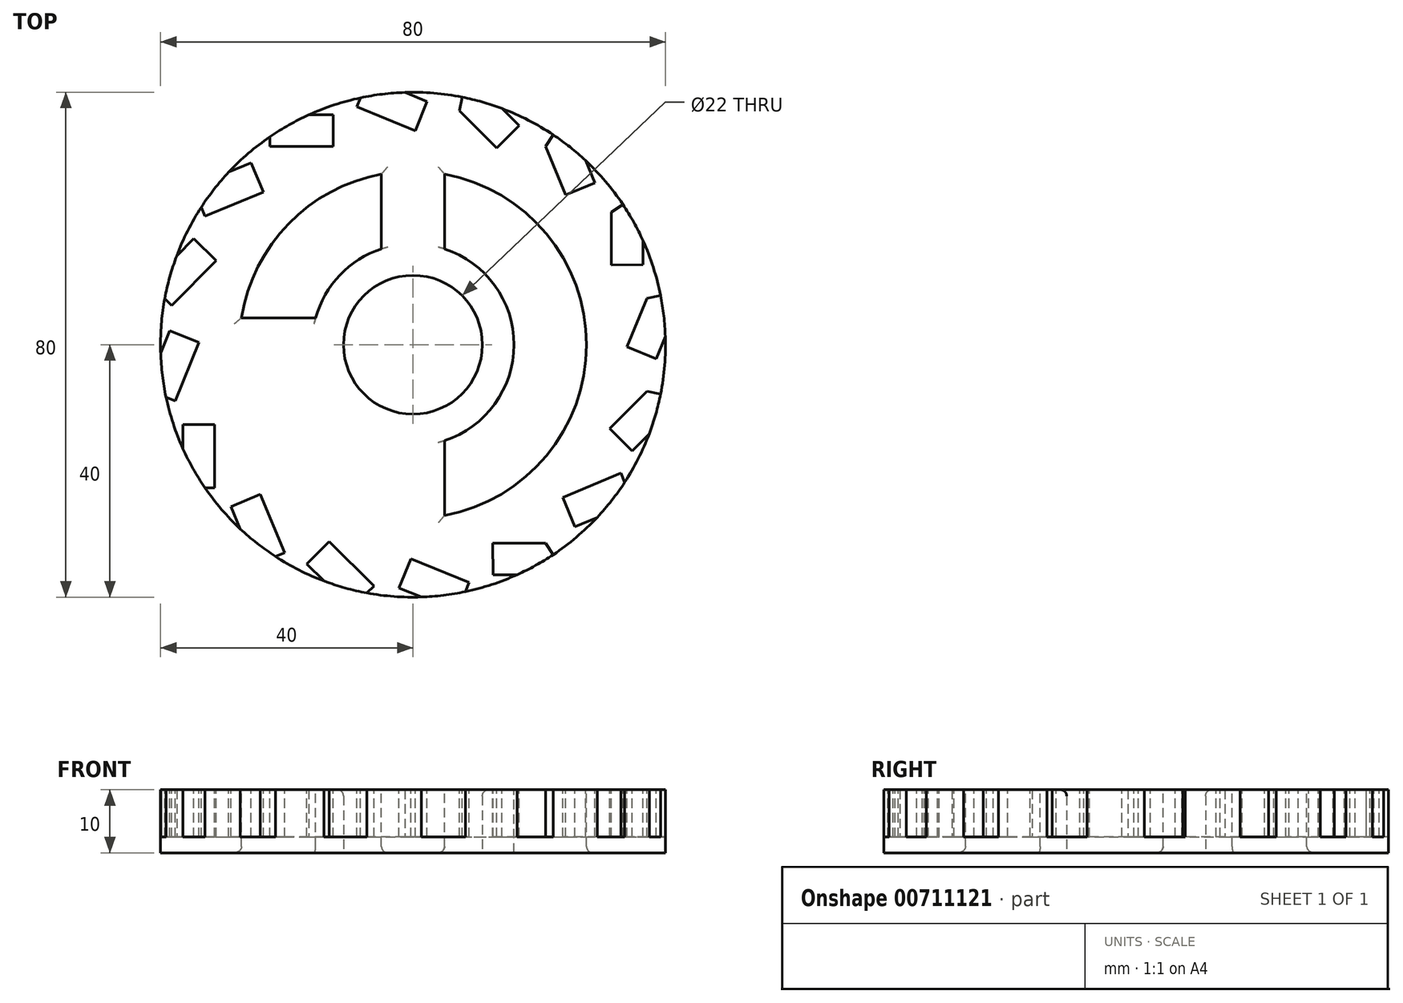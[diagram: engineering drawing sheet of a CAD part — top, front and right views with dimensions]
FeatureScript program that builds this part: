
annotation { "Feature Type Name" : "Feature", "Feature Type Description" : "" }
export const myFeature = defineFeature(function(context is Context, id is Id, definition is map)
    precondition{}
    {
        {
            var Q0;
            Q0=qCreatedBy(makeId("Front.planeOp"),FACE);
            var sketch = newSketch(context, id + "F0", { "sketchPlane" : qUnion([Q0])});
            skLineSegment(sketch, "E0.bottom", {"start": v(0, 0) * mm, "end": v(40, 0) * mm});
            skLineSegment(sketch, "E0.top", {"start": v(0, 10) * mm, "end": v(40, 10) * mm});
            skLineSegment(sketch, "E0.left", {"start": v(0, 0) * mm, "end": v(0, 10) * mm});
            skLineSegment(sketch, "E0.right", {"start": v(40, 0) * mm, "end": v(40, 10) * mm});
            skSolve(sketch);
        }
        {
            var Q0;
            Q0=makeQuery(id+"F0.imprint","IMPRINT",FACE,{"disambiguationData":[TD([[makeQuery(id+"F0.imprint","IMPRINT",EDGE,{"derivedFrom":sQuery(id+"F0.wireOp",EDGE,"E0.bottom")}),1.0]])]});
            var Q1;
            Q1=sQuery(id+"F0.wireOp",EDGE,"E0.left");
            revolve(context, id + "F1", {"surfaceOperationType" : NewSurfaceOperationType.NEW, "entities" : qUnion([Q0]), "axis" : qUnion([Q1]), "revolveType" : RevolveType.FULL});
        }
        {
            var Q0;
            Q0=makeQuery(id+"F1.opRevolve","SWEPT_FACE",FACE,{"disambiguationData":[OSD([sQuery(id+"F0.wireOp",EDGE,"E0.bottom")])]});
            var sketch = newSketch(context, id + "F2", { "sketchPlane" : qUnion([Q0])});
            skCircle(sketch, "E1", {"center": v(0, 0) * mm, "radius": 11 * mm});
            skSolve(sketch);
        }
        {
            var Q0;
            Q0=makeQuery(id+"F2.imprint","IMPRINT",FACE,{"disambiguationData":[TD([[makeQuery(id+"F2.imprint","IMPRINT",EDGE,{"derivedFrom":sQuery(id+"F2.wireOp",EDGE,"E1")}),1.0]])]});
            extrude(context, id + "F3", {"entities" : qUnion([Q0]), "operationType" : NewBodyOperationType.REMOVE, "oppositeDirection" : true, "depth" : 25 * mm, "offsetDistance" : 25 * mm});
        }
        {
            var Q0;
            Q0=makeQuery(id+"F1.opRevolve","SWEPT_FACE",FACE,{"disambiguationData":[OSD([sQuery(id+"F0.wireOp",EDGE,"E0.top")])]});
            var sketch = newSketch(context, id + "F4", { "sketchPlane" : qUnion([Q0])});
            skCircle(sketch, "E2.cCircle", {"center": v(0, 0) * mm, "radius": 40 * mm, "construction": true});
            skLineSegment(sketch, "E2.0", {"start": v(-7.96, 40) * mm, "end": v(7.96, 40) * mm});
            skLineSegment(sketch, "E2.1", {"start": v(7.96, 40) * mm, "end": v(22.66, 33.91) * mm});
            skLineSegment(sketch, "E2.2", {"start": v(22.66, 33.91) * mm, "end": v(33.91, 22.66) * mm});
            skLineSegment(sketch, "E2.3", {"start": v(33.91, 22.66) * mm, "end": v(40, 7.96) * mm});
            skLineSegment(sketch, "E2.4", {"start": v(40, 7.96) * mm, "end": v(40, -7.96) * mm});
            skLineSegment(sketch, "E2.5", {"start": v(40, -7.96) * mm, "end": v(33.91, -22.66) * mm});
            skLineSegment(sketch, "E2.6", {"start": v(33.91, -22.66) * mm, "end": v(22.66, -33.91) * mm});
            skLineSegment(sketch, "E2.7", {"start": v(22.66, -33.91) * mm, "end": v(7.96, -40) * mm});
            skLineSegment(sketch, "E2.8", {"start": v(7.96, -40) * mm, "end": v(-7.96, -40) * mm});
            skLineSegment(sketch, "E2.9", {"start": v(-7.96, -40) * mm, "end": v(-22.66, -33.91) * mm});
            skLineSegment(sketch, "E2.10", {"start": v(-22.66, -33.91) * mm, "end": v(-33.91, -22.66) * mm});
            skLineSegment(sketch, "E2.11", {"start": v(-33.91, -22.66) * mm, "end": v(-40, -7.96) * mm});
            skLineSegment(sketch, "E2.12", {"start": v(-40, -7.96) * mm, "end": v(-40, 7.96) * mm});
            skLineSegment(sketch, "E2.13", {"start": v(-40, 7.96) * mm, "end": v(-33.91, 22.66) * mm});
            skLineSegment(sketch, "E2.14", {"start": v(-33.91, 22.66) * mm, "end": v(-22.66, 33.91) * mm});
            skLineSegment(sketch, "E2.15", {"start": v(-22.66, 33.91) * mm, "end": v(-7.96, 40) * mm});
            skPoint(sketch, "E2.0.midPoint", {"position": v(0, 40) * mm});
            skLineSegment(sketch, "E3", {"start": v(-7.96, 40) * mm, "end": v(7.96, -40) * mm});
            skLineSegment(sketch, "E4", {"start": v(7.96, 40) * mm, "end": v(-7.96, -40) * mm});
            skLineSegment(sketch, "E5", {"start": v(22.66, 33.91) * mm, "end": v(-22.66, -33.91) * mm});
            skLineSegment(sketch, "E6", {"start": v(33.91, 22.66) * mm, "end": v(-33.91, -22.66) * mm});
            skLineSegment(sketch, "E7", {"start": v(40, 7.96) * mm, "end": v(-40, -7.96) * mm});
            skLineSegment(sketch, "E8", {"start": v(40, -7.96) * mm, "end": v(-40, 7.96) * mm});
            skLineSegment(sketch, "E9", {"start": v(-33.91, 22.66) * mm, "end": v(33.91, -22.66) * mm});
            skLineSegment(sketch, "E10", {"start": v(22.66, -33.91) * mm, "end": v(-22.66, 33.91) * mm});
            skLineSegment(sketch, "E11", {"start": v(-7.96, 40) * mm, "end": v(-7, 42.31) * mm});
            skLineSegment(sketch, "E12", {"start": v(-7, 42.31) * mm, "end": v(2.25, 38.53) * mm});
            skLineSegment(sketch, "E13", {"start": v(2.25, 38.53) * mm, "end": v(1.3, 36.21) * mm});
            skLineSegment(sketch, "E14", {"start": v(-7.96, 40) * mm, "end": v(-8.9, 37.69) * mm});
            skLineSegment(sketch, "E15", {"start": v(-8.9, 37.69) * mm, "end": v(0.35, 33.9) * mm});
            skLineSegment(sketch, "E16", {"start": v(0.35, 33.9) * mm, "end": v(1.3, 36.21) * mm});
            skCircle(sketch, "E17.0.0", {"center": v(0, 0) * mm, "radius": 40 * mm});
            skLineSegment(sketch, "E18.1.0", {"start": v(-22.67, 36.41) * mm, "end": v(-12.67, 36.45) * mm});
            skLineSegment(sketch, "E18.1.1", {"start": v(-22.66, 33.91) * mm, "end": v(-22.67, 36.41) * mm});
            skLineSegment(sketch, "E18.1.2", {"start": v(-22.66, 33.91) * mm, "end": v(-22.65, 31.41) * mm});
            skLineSegment(sketch, "E18.1.3", {"start": v(-22.65, 31.41) * mm, "end": v(-12.65, 31.45) * mm});
            skLineSegment(sketch, "E18.1.4", {"start": v(-12.65, 31.45) * mm, "end": v(-12.66, 33.95) * mm});
            skLineSegment(sketch, "E18.1.5", {"start": v(-12.67, 36.45) * mm, "end": v(-12.66, 33.95) * mm});
            skLineSegment(sketch, "E18.2.0", {"start": v(-34.88, 24.96) * mm, "end": v(-25.65, 28.83) * mm});
            skLineSegment(sketch, "E18.2.1", {"start": v(-33.91, 22.66) * mm, "end": v(-34.88, 24.96) * mm});
            skLineSegment(sketch, "E18.2.2", {"start": v(-33.91, 22.66) * mm, "end": v(-32.94, 20.35) * mm});
            skLineSegment(sketch, "E18.2.3", {"start": v(-32.94, 20.35) * mm, "end": v(-23.72, 24.22) * mm});
            skLineSegment(sketch, "E18.2.4", {"start": v(-23.72, 24.22) * mm, "end": v(-24.69, 26.52) * mm});
            skLineSegment(sketch, "E18.2.5", {"start": v(-25.65, 28.83) * mm, "end": v(-24.69, 26.52) * mm});
            skLineSegment(sketch, "E19.3.3.0", {"start": v(-40, 7.96) * mm, "end": v(-41.78, 9.72) * mm});
            skLineSegment(sketch, "E19.6.3.0", {"start": v(-40, 7.96) * mm, "end": v(-38.22, 6.2) * mm});
            skLineSegment(sketch, "E19.8.3.0", {"start": v(-41.78, 9.72) * mm, "end": v(-34.73, 16.82) * mm});
            skLineSegment(sketch, "E19.9.3.0", {"start": v(-38.22, 6.2) * mm, "end": v(-31.18, 13.3) * mm});
            skLineSegment(sketch, "E19.12.3.0", {"start": v(-31.18, 13.3) * mm, "end": v(-32.96, 15.06) * mm});
            skLineSegment(sketch, "E19.15.3.0", {"start": v(-34.73, 16.82) * mm, "end": v(-32.96, 15.06) * mm});
            skLineSegment(sketch, "E19.3.4.0", {"start": v(-40, -7.96) * mm, "end": v(-42.31, -7) * mm});
            skLineSegment(sketch, "E19.6.4.0", {"start": v(-40, -7.96) * mm, "end": v(-37.69, -8.9) * mm});
            skLineSegment(sketch, "E19.8.4.0", {"start": v(-42.31, -7) * mm, "end": v(-38.53, 2.25) * mm});
            skLineSegment(sketch, "E19.9.4.0", {"start": v(-37.69, -8.9) * mm, "end": v(-33.9, 0.35) * mm});
            skLineSegment(sketch, "E19.12.4.0", {"start": v(-33.9, 0.35) * mm, "end": v(-36.21, 1.3) * mm});
            skLineSegment(sketch, "E19.15.4.0", {"start": v(-38.53, 2.25) * mm, "end": v(-36.21, 1.3) * mm});
            skLineSegment(sketch, "E19.3.5.0", {"start": v(-33.91, -22.66) * mm, "end": v(-36.41, -22.67) * mm});
            skLineSegment(sketch, "E19.6.5.0", {"start": v(-33.91, -22.66) * mm, "end": v(-31.41, -22.65) * mm});
            skLineSegment(sketch, "E19.8.5.0", {"start": v(-36.41, -22.67) * mm, "end": v(-36.45, -12.67) * mm});
            skLineSegment(sketch, "E19.9.5.0", {"start": v(-31.41, -22.65) * mm, "end": v(-31.45, -12.65) * mm});
            skLineSegment(sketch, "E19.12.5.0", {"start": v(-31.45, -12.65) * mm, "end": v(-33.95, -12.66) * mm});
            skLineSegment(sketch, "E19.15.5.0", {"start": v(-36.45, -12.67) * mm, "end": v(-33.95, -12.66) * mm});
            skLineSegment(sketch, "E19.3.6.0", {"start": v(-22.66, -33.91) * mm, "end": v(-24.96, -34.88) * mm});
            skLineSegment(sketch, "E19.6.6.0", {"start": v(-22.66, -33.91) * mm, "end": v(-20.35, -32.94) * mm});
            skLineSegment(sketch, "E19.8.6.0", {"start": v(-24.96, -34.88) * mm, "end": v(-28.83, -25.65) * mm});
            skLineSegment(sketch, "E19.9.6.0", {"start": v(-20.35, -32.94) * mm, "end": v(-24.22, -23.72) * mm});
            skLineSegment(sketch, "E19.12.6.0", {"start": v(-24.22, -23.72) * mm, "end": v(-26.52, -24.69) * mm});
            skLineSegment(sketch, "E19.15.6.0", {"start": v(-28.83, -25.65) * mm, "end": v(-26.52, -24.69) * mm});
            skLineSegment(sketch, "E19.3.7.0", {"start": v(-7.96, -40) * mm, "end": v(-9.72, -41.78) * mm});
            skLineSegment(sketch, "E19.6.7.0", {"start": v(-7.96, -40) * mm, "end": v(-6.2, -38.22) * mm});
            skLineSegment(sketch, "E19.8.7.0", {"start": v(-9.72, -41.78) * mm, "end": v(-16.82, -34.73) * mm});
            skLineSegment(sketch, "E19.9.7.0", {"start": v(-6.2, -38.22) * mm, "end": v(-13.3, -31.18) * mm});
            skLineSegment(sketch, "E19.12.7.0", {"start": v(-13.3, -31.18) * mm, "end": v(-15.06, -32.96) * mm});
            skLineSegment(sketch, "E19.15.7.0", {"start": v(-16.82, -34.73) * mm, "end": v(-15.06, -32.96) * mm});
            skLineSegment(sketch, "E19.3.8.0", {"start": v(7.96, -40) * mm, "end": v(7, -42.31) * mm});
            skLineSegment(sketch, "E19.6.8.0", {"start": v(7.96, -40) * mm, "end": v(8.9, -37.69) * mm});
            skLineSegment(sketch, "E19.8.8.0", {"start": v(7, -42.31) * mm, "end": v(-2.25, -38.53) * mm});
            skLineSegment(sketch, "E19.9.8.0", {"start": v(8.9, -37.69) * mm, "end": v(-0.35, -33.9) * mm});
            skLineSegment(sketch, "E19.12.8.0", {"start": v(-0.35, -33.9) * mm, "end": v(-1.3, -36.21) * mm});
            skLineSegment(sketch, "E19.15.8.0", {"start": v(-2.25, -38.53) * mm, "end": v(-1.3, -36.21) * mm});
            skLineSegment(sketch, "E19.3.9.0", {"start": v(22.66, -33.91) * mm, "end": v(22.67, -36.41) * mm});
            skLineSegment(sketch, "E19.6.9.0", {"start": v(22.66, -33.91) * mm, "end": v(22.65, -31.41) * mm});
            skLineSegment(sketch, "E19.8.9.0", {"start": v(22.67, -36.41) * mm, "end": v(12.67, -36.45) * mm});
            skLineSegment(sketch, "E19.9.9.0", {"start": v(22.65, -31.41) * mm, "end": v(12.65, -31.45) * mm});
            skLineSegment(sketch, "E19.12.9.0", {"start": v(12.65, -31.45) * mm, "end": v(12.66, -33.95) * mm});
            skLineSegment(sketch, "E19.15.9.0", {"start": v(12.67, -36.45) * mm, "end": v(12.66, -33.95) * mm});
            skLineSegment(sketch, "E19.3.10.0", {"start": v(33.91, -22.66) * mm, "end": v(34.88, -24.96) * mm});
            skLineSegment(sketch, "E19.6.10.0", {"start": v(33.91, -22.66) * mm, "end": v(32.94, -20.35) * mm});
            skLineSegment(sketch, "E19.8.10.0", {"start": v(34.88, -24.96) * mm, "end": v(25.65, -28.83) * mm});
            skLineSegment(sketch, "E19.9.10.0", {"start": v(32.94, -20.35) * mm, "end": v(23.72, -24.22) * mm});
            skLineSegment(sketch, "E19.12.10.0", {"start": v(23.72, -24.22) * mm, "end": v(24.69, -26.52) * mm});
            skLineSegment(sketch, "E19.15.10.0", {"start": v(25.65, -28.83) * mm, "end": v(24.69, -26.52) * mm});
            skLineSegment(sketch, "E19.3.11.0", {"start": v(40, -7.96) * mm, "end": v(41.78, -9.72) * mm});
            skLineSegment(sketch, "E19.6.11.0", {"start": v(40, -7.96) * mm, "end": v(38.22, -6.2) * mm});
            skLineSegment(sketch, "E19.8.11.0", {"start": v(41.78, -9.72) * mm, "end": v(34.73, -16.82) * mm});
            skLineSegment(sketch, "E19.9.11.0", {"start": v(38.22, -6.2) * mm, "end": v(31.18, -13.3) * mm});
            skLineSegment(sketch, "E19.12.11.0", {"start": v(31.18, -13.3) * mm, "end": v(32.96, -15.06) * mm});
            skLineSegment(sketch, "E19.15.11.0", {"start": v(34.73, -16.82) * mm, "end": v(32.96, -15.06) * mm});
            skLineSegment(sketch, "E19.3.12.0", {"start": v(40, 7.96) * mm, "end": v(42.31, 7) * mm});
            skLineSegment(sketch, "E19.6.12.0", {"start": v(40, 7.96) * mm, "end": v(37.69, 8.9) * mm});
            skLineSegment(sketch, "E19.8.12.0", {"start": v(42.31, 7) * mm, "end": v(38.53, -2.25) * mm});
            skLineSegment(sketch, "E19.9.12.0", {"start": v(37.69, 8.9) * mm, "end": v(33.9, -0.35) * mm});
            skLineSegment(sketch, "E19.12.12.0", {"start": v(33.9, -0.35) * mm, "end": v(36.21, -1.3) * mm});
            skLineSegment(sketch, "E19.15.12.0", {"start": v(38.53, -2.25) * mm, "end": v(36.21, -1.3) * mm});
            skLineSegment(sketch, "E19.3.13.0", {"start": v(33.91, 22.66) * mm, "end": v(36.41, 22.67) * mm});
            skLineSegment(sketch, "E19.6.13.0", {"start": v(33.91, 22.66) * mm, "end": v(31.41, 22.65) * mm});
            skLineSegment(sketch, "E19.8.13.0", {"start": v(36.41, 22.67) * mm, "end": v(36.45, 12.67) * mm});
            skLineSegment(sketch, "E19.9.13.0", {"start": v(31.41, 22.65) * mm, "end": v(31.45, 12.65) * mm});
            skLineSegment(sketch, "E19.12.13.0", {"start": v(31.45, 12.65) * mm, "end": v(33.95, 12.66) * mm});
            skLineSegment(sketch, "E19.15.13.0", {"start": v(36.45, 12.67) * mm, "end": v(33.95, 12.66) * mm});
            skLineSegment(sketch, "E19.3.14.0", {"start": v(22.66, 33.91) * mm, "end": v(24.96, 34.88) * mm});
            skLineSegment(sketch, "E19.6.14.0", {"start": v(22.66, 33.91) * mm, "end": v(20.35, 32.94) * mm});
            skLineSegment(sketch, "E19.8.14.0", {"start": v(24.96, 34.88) * mm, "end": v(28.83, 25.65) * mm});
            skLineSegment(sketch, "E19.9.14.0", {"start": v(20.35, 32.94) * mm, "end": v(24.22, 23.72) * mm});
            skLineSegment(sketch, "E19.12.14.0", {"start": v(24.22, 23.72) * mm, "end": v(26.52, 24.69) * mm});
            skLineSegment(sketch, "E19.15.14.0", {"start": v(28.83, 25.65) * mm, "end": v(26.52, 24.69) * mm});
            skLineSegment(sketch, "E19.3.15.0", {"start": v(7.96, 40) * mm, "end": v(9.72, 41.78) * mm});
            skLineSegment(sketch, "E19.6.15.0", {"start": v(7.96, 40) * mm, "end": v(6.2, 38.22) * mm});
            skLineSegment(sketch, "E19.8.15.0", {"start": v(9.72, 41.78) * mm, "end": v(16.82, 34.73) * mm});
            skLineSegment(sketch, "E19.9.15.0", {"start": v(6.2, 38.22) * mm, "end": v(13.3, 31.18) * mm});
            skLineSegment(sketch, "E19.12.15.0", {"start": v(13.3, 31.18) * mm, "end": v(15.06, 32.96) * mm});
            skLineSegment(sketch, "E19.15.15.0", {"start": v(16.82, 34.73) * mm, "end": v(15.06, 32.96) * mm});
            skSolve(sketch);
        }
        {
            var Q0;
            {var subQ0=sQuery(id+"F4.wireOp",EDGE,"E13");Q0=makeQuery(id+"F4.imprint","IMPRINT",FACE,{"disambiguationData":[TD([[makeQuery(id+"F4.imprint","IMPRINT",EDGE,{"derivedFrom":subQ0}),-1.0]])]});}
            var Q1;
            {var subQ0=sQuery(id+"F4.wireOp",EDGE,"E15");var subQ5=sQuery(id+"F4.wireOp",EDGE,"E14");var subQ6=makeQuery(id+"F4.imprint","INTERSECT",VERTEX,{"derivedFrom":[subQ5,subQ0]});Q1=makeQuery(id+"F4.imprint","IMPRINT",FACE,{"disambiguationData":[TD([[makeQuery(id+"F4.imprint","IMPRINT",EDGE,{"disambiguationData":[TD([[subQ6,-1.0]])],"derivedFrom":subQ0}),1.0]])]});}
            var Q2;
            {var subQ0=sQuery(id+"F4.wireOp",EDGE,"E11");Q2=makeQuery(id+"F4.imprint","IMPRINT",FACE,{"disambiguationData":[TD([[makeQuery(id+"F4.imprint","IMPRINT",EDGE,{"derivedFrom":subQ0}),-1.0]])]});}
            var Q3;
            {var subQ1=sQuery(id+"F4.wireOp",EDGE,"E2.0");var subQ3=sQuery(id+"F4.wireOp",EDGE,"E12");var subQ4=makeQuery(id+"F4.imprint","INTERSECT",VERTEX,{"derivedFrom":[subQ1,subQ3]});Q3=makeQuery(id+"F4.imprint","IMPRINT",FACE,{"disambiguationData":[TD([[makeQuery(id+"F4.imprint","IMPRINT",EDGE,{"disambiguationData":[TD([[subQ4,-1.0]])],"derivedFrom":subQ3}),-1.0]])]});}
            var Q4;
            {var subQ1=sQuery(id+"F4.wireOp",EDGE,"E3");var subQ3=makeQuery(id+"F1.opRevolve","SWEPT_EDGE",EDGE,{"disambiguationData":[OSD([sQuery(id+"F0.wireOp",EDGE,"E0.top"),sQuery(id+"F0.wireOp",EDGE,"E0.right")])]});var subQ4=makeQuery(id+"F4.imprint","INTERSECT",VERTEX,{"disambiguationData":[OD(0.0)],"derivedFrom":[subQ3,subQ1]});Q4=makeQuery(id+"F4.imprint","IMPRINT",FACE,{"disambiguationData":[TD([[makeQuery(id+"F4.imprint","IMPRINT",EDGE,{"disambiguationData":[TD([[subQ4,1.0]])],"derivedFrom":subQ3}),1.0]])]});}
            var Q5;
            {var subQ0=sQuery(id+"F4.wireOp",EDGE,"E18.1.4");Q5=makeQuery(id+"F4.imprint","IMPRINT",FACE,{"disambiguationData":[TD([[makeQuery(id+"F4.imprint","IMPRINT",EDGE,{"derivedFrom":subQ0}),1.0]])]});}
            var Q6;
            {var subQ0=sQuery(id+"F4.wireOp",EDGE,"E18.1.1");Q6=makeQuery(id+"F4.imprint","IMPRINT",FACE,{"disambiguationData":[TD([[makeQuery(id+"F4.imprint","IMPRINT",EDGE,{"derivedFrom":subQ0}),-1.0]])]});}
            var Q7;
            {var subQ0=sQuery(id+"F4.wireOp",EDGE,"E10");var subQ5=sQuery(id+"F4.wireOp",EDGE,"E17.0.0");var subQ6=makeQuery(id+"F4.imprint","INTERSECT",VERTEX,{"disambiguationData":[OD(1.0)],"derivedFrom":[subQ0,subQ5]});Q7=makeQuery(id+"F4.imprint","IMPRINT",FACE,{"disambiguationData":[TD([[makeQuery(id+"F4.imprint","IMPRINT",EDGE,{"disambiguationData":[TD([[subQ6,-1.0]])],"derivedFrom":subQ5}),1.0]])]});}
            var Q8;
            {var subQ1=sQuery(id+"F4.wireOp",EDGE,"E10");var subQ3=sQuery(id+"F4.wireOp",EDGE,"E17.0.0");var subQ4=makeQuery(id+"F4.imprint","INTERSECT",VERTEX,{"disambiguationData":[OD(1.0)],"derivedFrom":[subQ1,subQ3]});Q8=makeQuery(id+"F4.imprint","IMPRINT",FACE,{"disambiguationData":[TD([[makeQuery(id+"F4.imprint","IMPRINT",EDGE,{"disambiguationData":[TD([[subQ4,1.0]])],"derivedFrom":subQ3}),1.0]])]});}
            var Q9;
            {var subQ0=sQuery(id+"F4.wireOp",EDGE,"E18.1.3");var subQ1=sQuery(id+"F4.wireOp",EDGE,"E10");var subQ2=makeQuery(id+"F4.imprint","INTERSECT",VERTEX,{"derivedFrom":[subQ1,subQ0]});Q9=makeQuery(id+"F4.imprint","IMPRINT",FACE,{"disambiguationData":[TD([[makeQuery(id+"F4.imprint","IMPRINT",EDGE,{"disambiguationData":[TD([[subQ2,-1.0]])],"derivedFrom":subQ1}),1.0]])]});}
            var Q10;
            {var subQ0=sQuery(id+"F4.wireOp",EDGE,"E19.12.15.0");Q10=makeQuery(id+"F4.imprint","IMPRINT",FACE,{"disambiguationData":[TD([[makeQuery(id+"F4.imprint","IMPRINT",EDGE,{"derivedFrom":subQ0}),1.0]])]});}
            var Q11;
            {var subQ0=sQuery(id+"F4.wireOp",EDGE,"E17.0.0");var subQ1=sQuery(id+"F4.wireOp",EDGE,"E4");var subQ2=makeQuery(id+"F4.imprint","INTERSECT",VERTEX,{"disambiguationData":[OD(0.0)],"derivedFrom":[subQ1,subQ0]});Q11=makeQuery(id+"F4.imprint","IMPRINT",FACE,{"disambiguationData":[TD([[makeQuery(id+"F4.imprint","IMPRINT",EDGE,{"disambiguationData":[TD([[subQ2,-1.0]])],"derivedFrom":subQ1}),-1.0]])]});}
            var Q12;
            {var subQ0=sQuery(id+"F4.wireOp",EDGE,"E18.2.4");Q12=makeQuery(id+"F4.imprint","IMPRINT",FACE,{"disambiguationData":[TD([[makeQuery(id+"F4.imprint","IMPRINT",EDGE,{"derivedFrom":subQ0}),1.0]])]});}
            var Q13;
            {var subQ0=sQuery(id+"F4.wireOp",EDGE,"E17.0.0");var subQ1=sQuery(id+"F4.wireOp",EDGE,"E9");var subQ2=makeQuery(id+"F4.imprint","INTERSECT",VERTEX,{"disambiguationData":[OD(0.0)],"derivedFrom":[subQ1,subQ0]});Q13=makeQuery(id+"F4.imprint","IMPRINT",FACE,{"disambiguationData":[TD([[makeQuery(id+"F4.imprint","IMPRINT",EDGE,{"disambiguationData":[TD([[subQ2,-1.0]])],"derivedFrom":subQ1}),-1.0]])]});}
            var Q14;
            {var subQ0=sQuery(id+"F4.wireOp",EDGE,"E19.12.14.0");Q14=makeQuery(id+"F4.imprint","IMPRINT",FACE,{"disambiguationData":[TD([[makeQuery(id+"F4.imprint","IMPRINT",EDGE,{"derivedFrom":subQ0}),1.0]])]});}
            var Q15;
            {var subQ4=sQuery(id+"F4.wireOp",EDGE,"E19.12.13.0");Q15=makeQuery(id+"F4.imprint","IMPRINT",FACE,{"disambiguationData":[TD([[makeQuery(id+"F4.imprint","IMPRINT",EDGE,{"derivedFrom":subQ4}),1.0]])]});}
            var Q16;
            {var subQ0=sQuery(id+"F4.wireOp",EDGE,"E19.12.12.0");Q16=makeQuery(id+"F4.imprint","IMPRINT",FACE,{"disambiguationData":[TD([[makeQuery(id+"F4.imprint","IMPRINT",EDGE,{"derivedFrom":subQ0}),1.0]])]});}
            var Q17;
            {var subQ0=sQuery(id+"F4.wireOp",EDGE,"E19.12.11.0");Q17=makeQuery(id+"F4.imprint","IMPRINT",FACE,{"disambiguationData":[TD([[makeQuery(id+"F4.imprint","IMPRINT",EDGE,{"derivedFrom":subQ0}),1.0]])]});}
            var Q18;
            {var subQ0=sQuery(id+"F4.wireOp",EDGE,"E19.12.10.0");Q18=makeQuery(id+"F4.imprint","IMPRINT",FACE,{"disambiguationData":[TD([[makeQuery(id+"F4.imprint","IMPRINT",EDGE,{"derivedFrom":subQ0}),1.0]])]});}
            var Q19;
            {var subQ0=sQuery(id+"F4.wireOp",EDGE,"E19.12.9.0");Q19=makeQuery(id+"F4.imprint","IMPRINT",FACE,{"disambiguationData":[TD([[makeQuery(id+"F4.imprint","IMPRINT",EDGE,{"derivedFrom":subQ0}),1.0]])]});}
            var Q20;
            {var subQ4=sQuery(id+"F4.wireOp",EDGE,"E19.12.8.0");Q20=makeQuery(id+"F4.imprint","IMPRINT",FACE,{"disambiguationData":[TD([[makeQuery(id+"F4.imprint","IMPRINT",EDGE,{"derivedFrom":subQ4}),1.0]])]});}
            var Q21;
            {var subQ0=sQuery(id+"F4.wireOp",EDGE,"E19.12.7.0");Q21=makeQuery(id+"F4.imprint","IMPRINT",FACE,{"disambiguationData":[TD([[makeQuery(id+"F4.imprint","IMPRINT",EDGE,{"derivedFrom":subQ0}),1.0]])]});}
            var Q22;
            {var subQ0=sQuery(id+"F4.wireOp",EDGE,"E19.12.6.0");Q22=makeQuery(id+"F4.imprint","IMPRINT",FACE,{"disambiguationData":[TD([[makeQuery(id+"F4.imprint","IMPRINT",EDGE,{"derivedFrom":subQ0}),1.0]])]});}
            var Q23;
            {var subQ6=sQuery(id+"F4.wireOp",EDGE,"E19.12.5.0");Q23=makeQuery(id+"F4.imprint","IMPRINT",FACE,{"disambiguationData":[TD([[makeQuery(id+"F4.imprint","IMPRINT",EDGE,{"derivedFrom":subQ6}),1.0]])]});}
            var Q24;
            {var subQ0=sQuery(id+"F4.wireOp",EDGE,"E19.12.4.0");Q24=makeQuery(id+"F4.imprint","IMPRINT",FACE,{"disambiguationData":[TD([[makeQuery(id+"F4.imprint","IMPRINT",EDGE,{"derivedFrom":subQ0}),1.0]])]});}
            var Q25;
            {var subQ0=sQuery(id+"F4.wireOp",EDGE,"E19.12.3.0");Q25=makeQuery(id+"F4.imprint","IMPRINT",FACE,{"disambiguationData":[TD([[makeQuery(id+"F4.imprint","IMPRINT",EDGE,{"derivedFrom":subQ0}),1.0]])]});}
            var Q26;
            {var subQ0=sQuery(id+"F4.wireOp",EDGE,"E19.9.3.0");var subQ1=sQuery(id+"F4.wireOp",EDGE,"E8");var subQ2=makeQuery(id+"F4.imprint","INTERSECT",VERTEX,{"derivedFrom":[subQ1,subQ0]});Q26=makeQuery(id+"F4.imprint","IMPRINT",FACE,{"disambiguationData":[TD([[makeQuery(id+"F4.imprint","IMPRINT",EDGE,{"disambiguationData":[TD([[subQ2,-1.0]])],"derivedFrom":subQ1}),1.0]])]});}
            var Q27;
            {var subQ0=sQuery(id+"F4.wireOp",EDGE,"E19.9.4.0");var subQ1=sQuery(id+"F4.wireOp",EDGE,"E7");var subQ2=makeQuery(id+"F4.imprint","INTERSECT",VERTEX,{"derivedFrom":[subQ1,subQ0]});Q27=makeQuery(id+"F4.imprint","IMPRINT",FACE,{"disambiguationData":[TD([[makeQuery(id+"F4.imprint","IMPRINT",EDGE,{"disambiguationData":[TD([[subQ2,-1.0]])],"derivedFrom":subQ1}),1.0]])]});}
            var Q28;
            {var subQ0=sQuery(id+"F4.wireOp",EDGE,"E19.9.5.0");var subQ1=sQuery(id+"F4.wireOp",EDGE,"E6");var subQ2=makeQuery(id+"F4.imprint","INTERSECT",VERTEX,{"derivedFrom":[subQ1,subQ0]});Q28=makeQuery(id+"F4.imprint","IMPRINT",FACE,{"disambiguationData":[TD([[makeQuery(id+"F4.imprint","IMPRINT",EDGE,{"disambiguationData":[TD([[subQ2,-1.0]])],"derivedFrom":subQ1}),1.0]])]});}
            var Q29;
            {var subQ0=sQuery(id+"F4.wireOp",EDGE,"E19.9.6.0");var subQ1=sQuery(id+"F4.wireOp",EDGE,"E5");var subQ2=makeQuery(id+"F4.imprint","INTERSECT",VERTEX,{"derivedFrom":[subQ1,subQ0]});Q29=makeQuery(id+"F4.imprint","IMPRINT",FACE,{"disambiguationData":[TD([[makeQuery(id+"F4.imprint","IMPRINT",EDGE,{"disambiguationData":[TD([[subQ2,-1.0]])],"derivedFrom":subQ1}),1.0]])]});}
            var Q30;
            {var subQ0=sQuery(id+"F4.wireOp",EDGE,"E19.9.7.0");var subQ1=sQuery(id+"F4.wireOp",EDGE,"E4");var subQ2=makeQuery(id+"F4.imprint","INTERSECT",VERTEX,{"derivedFrom":[subQ1,subQ0]});Q30=makeQuery(id+"F4.imprint","IMPRINT",FACE,{"disambiguationData":[TD([[makeQuery(id+"F4.imprint","IMPRINT",EDGE,{"disambiguationData":[TD([[subQ2,-1.0]])],"derivedFrom":subQ1}),1.0]])]});}
            var Q31;
            {var subQ0=sQuery(id+"F4.wireOp",EDGE,"E19.9.8.0");var subQ1=sQuery(id+"F4.wireOp",EDGE,"E3");var subQ2=makeQuery(id+"F4.imprint","INTERSECT",VERTEX,{"derivedFrom":[subQ1,subQ0]});Q31=makeQuery(id+"F4.imprint","IMPRINT",FACE,{"disambiguationData":[TD([[makeQuery(id+"F4.imprint","IMPRINT",EDGE,{"disambiguationData":[TD([[subQ2,-1.0]])],"derivedFrom":subQ1}),1.0]])]});}
            var Q32;
            {var subQ0=sQuery(id+"F4.wireOp",EDGE,"E17.0.0");var subQ1=sQuery(id+"F4.wireOp",EDGE,"E10");var subQ2=makeQuery(id+"F4.imprint","INTERSECT",VERTEX,{"disambiguationData":[OD(0.0)],"derivedFrom":[subQ1,subQ0]});Q32=makeQuery(id+"F4.imprint","IMPRINT",FACE,{"disambiguationData":[TD([[makeQuery(id+"F4.imprint","IMPRINT",EDGE,{"disambiguationData":[TD([[subQ2,-1.0]])],"derivedFrom":subQ1}),-1.0]])]});}
            var Q33;
            {var subQ0=sQuery(id+"F4.wireOp",EDGE,"E19.9.10.0");var subQ1=sQuery(id+"F4.wireOp",EDGE,"E9");var subQ2=makeQuery(id+"F4.imprint","INTERSECT",VERTEX,{"derivedFrom":[subQ1,subQ0]});Q33=makeQuery(id+"F4.imprint","IMPRINT",FACE,{"disambiguationData":[TD([[makeQuery(id+"F4.imprint","IMPRINT",EDGE,{"disambiguationData":[TD([[subQ2,-1.0]])],"derivedFrom":subQ1}),1.0]])]});}
            var Q34;
            {var subQ0=sQuery(id+"F4.wireOp",EDGE,"E17.0.0");var subQ1=sQuery(id+"F4.wireOp",EDGE,"E8");var subQ2=makeQuery(id+"F4.imprint","INTERSECT",VERTEX,{"disambiguationData":[OD(0.0)],"derivedFrom":[subQ1,subQ0]});Q34=makeQuery(id+"F4.imprint","IMPRINT",FACE,{"disambiguationData":[TD([[makeQuery(id+"F4.imprint","IMPRINT",EDGE,{"disambiguationData":[TD([[subQ2,-1.0]])],"derivedFrom":subQ1}),-1.0]])]});}
            var Q35;
            {var subQ0=sQuery(id+"F4.wireOp",EDGE,"E17.0.0");var subQ1=sQuery(id+"F4.wireOp",EDGE,"E7");var subQ2=makeQuery(id+"F4.imprint","INTERSECT",VERTEX,{"disambiguationData":[OD(0.0)],"derivedFrom":[subQ1,subQ0]});Q35=makeQuery(id+"F4.imprint","IMPRINT",FACE,{"disambiguationData":[TD([[makeQuery(id+"F4.imprint","IMPRINT",EDGE,{"disambiguationData":[TD([[subQ2,-1.0]])],"derivedFrom":subQ1}),-1.0]])]});}
            var Q36;
            {var subQ0=sQuery(id+"F4.wireOp",EDGE,"E17.0.0");var subQ1=sQuery(id+"F4.wireOp",EDGE,"E6");var subQ2=makeQuery(id+"F4.imprint","INTERSECT",VERTEX,{"disambiguationData":[OD(0.0)],"derivedFrom":[subQ1,subQ0]});Q36=makeQuery(id+"F4.imprint","IMPRINT",FACE,{"disambiguationData":[TD([[makeQuery(id+"F4.imprint","IMPRINT",EDGE,{"disambiguationData":[TD([[subQ2,-1.0]])],"derivedFrom":subQ1}),-1.0]])]});}
            var Q37;
            {var subQ0=sQuery(id+"F4.wireOp",EDGE,"E17.0.0");var subQ1=sQuery(id+"F4.wireOp",EDGE,"E5");var subQ2=makeQuery(id+"F4.imprint","INTERSECT",VERTEX,{"disambiguationData":[OD(0.0)],"derivedFrom":[subQ1,subQ0]});Q37=makeQuery(id+"F4.imprint","IMPRINT",FACE,{"disambiguationData":[TD([[makeQuery(id+"F4.imprint","IMPRINT",EDGE,{"disambiguationData":[TD([[subQ2,-1.0]])],"derivedFrom":subQ1}),-1.0]])]});}
            extrude(context, id + "F5", {"entities" : qUnion([Q0, Q1, Q2, Q3, Q4, Q5, Q6, Q7, Q8, Q9, Q10, Q11, Q12, Q13, Q14, Q15, Q16, Q17, Q18, Q19, Q20, Q21, Q22, Q23, Q24, Q25, Q26, Q27, Q28, Q29, Q30, Q31, Q32, Q33, Q34, Q35, Q36, Q37]), "operationType" : NewBodyOperationType.REMOVE, "oppositeDirection" : true, "depth" : 7.5 * mm, "offsetDistance" : 25 * mm});
        }
        {
            var Q0;
            Q0=makeQuery(id+"F1.opRevolve","SWEPT_FACE",FACE,{"disambiguationData":[OSD([sQuery(id+"F0.wireOp",EDGE,"E0.top")])]});
            var sketch = newSketch(context, id + "F6", { "sketchPlane" : qUnion([Q0])});
            skCircle(sketch, "E20", {"center": v(0, 0) * mm, "radius": 27.5 * mm});
            skCircle(sketch, "E21", {"center": v(0, 0) * mm, "radius": 16 * mm});
            skPoint(sketch, "E22", {"position": v(0, 27.5) * mm});
            skPoint(sketch, "E23", {"position": v(-27.5, 0) * mm});
            skLineSegment(sketch, "E24.bottom", {"start": v(5, 27.5) * mm, "end": v(-5, 27.5) * mm});
            skLineSegment(sketch, "E24.top", {"start": v(5, -27.5) * mm, "end": v(-5, -27.5) * mm});
            skLineSegment(sketch, "E24.left", {"start": v(5, 27.5) * mm, "end": v(5, -27.5) * mm});
            skLineSegment(sketch, "E24.right", {"start": v(-5, 27.5) * mm, "end": v(-5, -27.5) * mm});
            skLineSegment(sketch, "E25.bottom", {"start": v(27.5, 4.28) * mm, "end": v(-27.5, 4.28) * mm});
            skLineSegment(sketch, "E25.top", {"start": v(27.5, -4.28) * mm, "end": v(-27.5, -4.28) * mm});
            skLineSegment(sketch, "E25.left", {"start": v(27.5, 4.28) * mm, "end": v(27.5, -4.28) * mm});
            skLineSegment(sketch, "E25.right", {"start": v(-27.5, 4.28) * mm, "end": v(-27.5, -4.28) * mm});
            skPoint(sketch, "E25.cornerSnap0", {"position": v(35.8, 4.28) * mm});
            skSolve(sketch);
        }
        {
            var Q0;
            {var subQ0=sQuery(id+"F6.wireOp",EDGE,"E25.bottom");var subQ1=sQuery(id+"F6.wireOp",EDGE,"E20");var subQ2=makeQuery(id+"F6.imprint","INTERSECT",VERTEX,{"disambiguationData":[OD(0.0)],"derivedFrom":[subQ1,subQ0]});Q0=makeQuery(id+"F6.imprint","IMPRINT",FACE,{"disambiguationData":[TD([[makeQuery(id+"F6.imprint","IMPRINT",EDGE,{"disambiguationData":[TD([[subQ2,-1.0]])],"derivedFrom":subQ1}),1.0]])]});}
            var Q1;
            {var subQ0=sQuery(id+"F6.wireOp",EDGE,"E25.top");var subQ1=sQuery(id+"F6.wireOp",EDGE,"E20");var subQ2=makeQuery(id+"F6.imprint","INTERSECT",VERTEX,{"disambiguationData":[OD(0.0)],"derivedFrom":[subQ1,subQ0]});Q1=makeQuery(id+"F6.imprint","IMPRINT",FACE,{"disambiguationData":[TD([[makeQuery(id+"F6.imprint","IMPRINT",EDGE,{"disambiguationData":[TD([[subQ2,-1.0]])],"derivedFrom":subQ1}),1.0]])]});}
            var Q2;
            {var subQ0=sQuery(id+"F6.wireOp",EDGE,"E24.left");var subQ1=sQuery(id+"F6.wireOp",EDGE,"E20");var subQ2=makeQuery(id+"F6.imprint","INTERSECT",VERTEX,{"disambiguationData":[OD(1.0)],"derivedFrom":[subQ1,subQ0]});Q2=makeQuery(id+"F6.imprint","IMPRINT",FACE,{"disambiguationData":[TD([[makeQuery(id+"F6.imprint","IMPRINT",EDGE,{"disambiguationData":[TD([[subQ2,-1.0]])],"derivedFrom":subQ1}),1.0]])]});}
            var Q3;
            {var subQ0=sQuery(id+"F6.wireOp",EDGE,"E24.right");var subQ1=sQuery(id+"F6.wireOp",EDGE,"E20");var subQ2=makeQuery(id+"F6.imprint","INTERSECT",VERTEX,{"disambiguationData":[OD(0.0)],"derivedFrom":[subQ1,subQ0]});Q3=makeQuery(id+"F6.imprint","IMPRINT",FACE,{"disambiguationData":[TD([[makeQuery(id+"F6.imprint","IMPRINT",EDGE,{"disambiguationData":[TD([[subQ2,-1.0]])],"derivedFrom":subQ1}),1.0]])]});}
            extrude(context, id + "F7", {"entities" : qUnion([Q0, Q1, Q2, Q3]), "operationType" : NewBodyOperationType.REMOVE, "oppositeDirection" : true, "depth" : 25 * mm, "offsetDistance" : 25 * mm});
        }
        {
            var Q0;
            Q0=makeQuery(id+"F3.boolean.opBoolean","INTERSECT",EDGE,{"derivedFrom":[makeQuery(id+"F1.opRevolve","SWEPT_FACE",FACE,{"disambiguationData":[OSD([sQuery(id+"F0.wireOp",EDGE,"E0.top")])]}),makeQuery(id+"F3.opExtrude","SWEPT_FACE",FACE,{"disambiguationData":[OSD([sQuery(id+"F2.wireOp",EDGE,"E1")])]})]});
            var Q1;
            Q1=makeQuery(id+"F3.boolean.opBoolean","COPY",EDGE,{"derivedFrom":makeQuery(id+"F3.opExtrude","CAP_EDGE",EDGE,{"disambiguationData":[OSD([sQuery(id+"F2.wireOp",EDGE,"E1")])],"isStart":true})});
            var Q2;
            {var subQ0=sQuery(id+"F6.wireOp",EDGE,"E21");Q2=makeQuery(id+"F7.boolean.opBoolean","COPY",EDGE,{"derivedFrom":makeQuery(id+"F7.opExtrude","CAP_EDGE",EDGE,{"disambiguationData":[OSD([subQ0]),TDD([makeQuery(id+"F6.imprint","IMPRINT",EDGE,{"disambiguationData":[TD([[makeQuery(id+"F6.imprint","INTERSECT",VERTEX,{"disambiguationData":[OD(0.0)],"derivedFrom":[subQ0,sQuery(id+"F6.wireOp",EDGE,"E25.top")]}),-1.0]])],"derivedFrom":subQ0})])],"isStart":true})});}
            var Q3;
            {var subQ0=sQuery(id+"F6.wireOp",EDGE,"E24.right");Q3=makeQuery(id+"F7.boolean.opBoolean","COPY",EDGE,{"derivedFrom":makeQuery(id+"F7.opExtrude","CAP_EDGE",EDGE,{"disambiguationData":[OSD([subQ0]),TDD([makeQuery(id+"F6.imprint","IMPRINT",EDGE,{"disambiguationData":[TD([[makeQuery(id+"F6.imprint","INTERSECT",VERTEX,{"disambiguationData":[OD(1.0)],"derivedFrom":[sQuery(id+"F6.wireOp",EDGE,"E20"),subQ0]}),1.0]])],"derivedFrom":subQ0})])],"isStart":true})});}
            var Q4;
            {var subQ0=sQuery(id+"F6.wireOp",EDGE,"E20");Q4=makeQuery(id+"F7.boolean.opBoolean","COPY",EDGE,{"derivedFrom":makeQuery(id+"F7.opExtrude","CAP_EDGE",EDGE,{"disambiguationData":[OSD([subQ0]),TDD([makeQuery(id+"F6.imprint","IMPRINT",EDGE,{"disambiguationData":[TD([[makeQuery(id+"F6.imprint","INTERSECT",VERTEX,{"disambiguationData":[OD(0.0)],"derivedFrom":[subQ0,sQuery(id+"F6.wireOp",EDGE,"E25.top")]}),-1.0]])],"derivedFrom":subQ0})])],"isStart":true})});}
            var Q5;
            {var subQ0=sQuery(id+"F6.wireOp",EDGE,"E25.top");Q5=makeQuery(id+"F7.boolean.opBoolean","COPY",EDGE,{"derivedFrom":makeQuery(id+"F7.opExtrude","CAP_EDGE",EDGE,{"disambiguationData":[OSD([subQ0]),TDD([makeQuery(id+"F6.imprint","IMPRINT",EDGE,{"disambiguationData":[TD([[makeQuery(id+"F6.imprint","INTERSECT",VERTEX,{"disambiguationData":[OD(0.0)],"derivedFrom":[sQuery(id+"F6.wireOp",EDGE,"E20"),subQ0]}),1.0]])],"derivedFrom":subQ0})])],"isStart":true})});}
            var Q6;
            {var subQ0=sQuery(id+"F6.wireOp",EDGE,"E24.left");Q6=makeQuery(id+"F7.boolean.opBoolean","COPY",EDGE,{"derivedFrom":makeQuery(id+"F7.opExtrude","CAP_EDGE",EDGE,{"disambiguationData":[OSD([subQ0]),TDD([makeQuery(id+"F6.imprint","IMPRINT",EDGE,{"disambiguationData":[TD([[makeQuery(id+"F6.imprint","INTERSECT",VERTEX,{"disambiguationData":[OD(1.0)],"derivedFrom":[sQuery(id+"F6.wireOp",EDGE,"E20"),subQ0]}),1.0]])],"derivedFrom":subQ0})])],"isStart":true})});}
            var Q7;
            {var subQ0=sQuery(id+"F6.wireOp",EDGE,"E20");Q7=makeQuery(id+"F7.boolean.opBoolean","COPY",EDGE,{"derivedFrom":makeQuery(id+"F7.opExtrude","CAP_EDGE",EDGE,{"disambiguationData":[OSD([subQ0]),TDD([makeQuery(id+"F6.imprint","IMPRINT",EDGE,{"disambiguationData":[TD([[makeQuery(id+"F6.imprint","INTERSECT",VERTEX,{"disambiguationData":[OD(1.0)],"derivedFrom":[subQ0,sQuery(id+"F6.wireOp",EDGE,"E24.left")]}),-1.0]])],"derivedFrom":subQ0})])],"isStart":true})});}
            var Q8;
            {var subQ0=sQuery(id+"F6.wireOp",EDGE,"E25.top");Q8=makeQuery(id+"F7.boolean.opBoolean","COPY",EDGE,{"derivedFrom":makeQuery(id+"F7.opExtrude","CAP_EDGE",EDGE,{"disambiguationData":[OSD([subQ0]),TDD([makeQuery(id+"F6.imprint","IMPRINT",EDGE,{"disambiguationData":[TD([[makeQuery(id+"F6.imprint","INTERSECT",VERTEX,{"disambiguationData":[OD(1.0)],"derivedFrom":[sQuery(id+"F6.wireOp",EDGE,"E20"),subQ0]}),-1.0]])],"derivedFrom":subQ0})])],"isStart":true})});}
            var Q9;
            {var subQ0=sQuery(id+"F6.wireOp",EDGE,"E21");Q9=makeQuery(id+"F7.boolean.opBoolean","COPY",EDGE,{"derivedFrom":makeQuery(id+"F7.opExtrude","CAP_EDGE",EDGE,{"disambiguationData":[OSD([subQ0]),TDD([makeQuery(id+"F6.imprint","IMPRINT",EDGE,{"disambiguationData":[TD([[makeQuery(id+"F6.imprint","INTERSECT",VERTEX,{"disambiguationData":[OD(1.0)],"derivedFrom":[subQ0,sQuery(id+"F6.wireOp",EDGE,"E24.left")]}),-1.0]])],"derivedFrom":subQ0})])],"isStart":true})});}
            var Q10;
            {var subQ0=sQuery(id+"F6.wireOp",EDGE,"E25.bottom");Q10=makeQuery(id+"F7.boolean.opBoolean","COPY",EDGE,{"derivedFrom":makeQuery(id+"F7.opExtrude","CAP_EDGE",EDGE,{"disambiguationData":[OSD([subQ0]),TDD([makeQuery(id+"F6.imprint","IMPRINT",EDGE,{"disambiguationData":[TD([[makeQuery(id+"F6.imprint","INTERSECT",VERTEX,{"disambiguationData":[OD(1.0)],"derivedFrom":[sQuery(id+"F6.wireOp",EDGE,"E20"),subQ0]}),1.0]])],"derivedFrom":subQ0})])],"isStart":true})});}
            var Q11;
            {var subQ0=sQuery(id+"F6.wireOp",EDGE,"E20");Q11=makeQuery(id+"F7.boolean.opBoolean","COPY",EDGE,{"derivedFrom":makeQuery(id+"F7.opExtrude","CAP_EDGE",EDGE,{"disambiguationData":[OSD([subQ0]),TDD([makeQuery(id+"F6.imprint","IMPRINT",EDGE,{"disambiguationData":[TD([[makeQuery(id+"F6.imprint","INTERSECT",VERTEX,{"disambiguationData":[OD(0.0)],"derivedFrom":[subQ0,sQuery(id+"F6.wireOp",EDGE,"E24.right")]}),-1.0]])],"derivedFrom":subQ0})])],"isStart":true})});}
            var Q12;
            {var subQ0=sQuery(id+"F6.wireOp",EDGE,"E21");Q12=makeQuery(id+"F7.boolean.opBoolean","COPY",EDGE,{"derivedFrom":makeQuery(id+"F7.opExtrude","CAP_EDGE",EDGE,{"disambiguationData":[OSD([subQ0]),TDD([makeQuery(id+"F6.imprint","IMPRINT",EDGE,{"disambiguationData":[TD([[makeQuery(id+"F6.imprint","INTERSECT",VERTEX,{"disambiguationData":[OD(0.0)],"derivedFrom":[subQ0,sQuery(id+"F6.wireOp",EDGE,"E24.right")]}),-1.0]])],"derivedFrom":subQ0})])],"isStart":true})});}
            var Q13;
            {var subQ0=sQuery(id+"F6.wireOp",EDGE,"E24.right");Q13=makeQuery(id+"F7.boolean.opBoolean","COPY",EDGE,{"derivedFrom":makeQuery(id+"F7.opExtrude","CAP_EDGE",EDGE,{"disambiguationData":[OSD([subQ0]),TDD([makeQuery(id+"F6.imprint","IMPRINT",EDGE,{"disambiguationData":[TD([[makeQuery(id+"F6.imprint","INTERSECT",VERTEX,{"disambiguationData":[OD(0.0)],"derivedFrom":[sQuery(id+"F6.wireOp",EDGE,"E20"),subQ0]}),-1.0]])],"derivedFrom":subQ0})])],"isStart":true})});}
            var Q14;
            {var subQ0=sQuery(id+"F6.wireOp",EDGE,"E24.left");Q14=makeQuery(id+"F7.boolean.opBoolean","COPY",EDGE,{"derivedFrom":makeQuery(id+"F7.opExtrude","CAP_EDGE",EDGE,{"disambiguationData":[OSD([subQ0]),TDD([makeQuery(id+"F6.imprint","IMPRINT",EDGE,{"disambiguationData":[TD([[makeQuery(id+"F6.imprint","INTERSECT",VERTEX,{"disambiguationData":[OD(0.0)],"derivedFrom":[sQuery(id+"F6.wireOp",EDGE,"E20"),subQ0]}),-1.0]])],"derivedFrom":subQ0})])],"isStart":true})});}
            var Q15;
            {var subQ0=sQuery(id+"F6.wireOp",EDGE,"E21");Q15=makeQuery(id+"F7.boolean.opBoolean","COPY",EDGE,{"derivedFrom":makeQuery(id+"F7.opExtrude","CAP_EDGE",EDGE,{"disambiguationData":[OSD([subQ0]),TDD([makeQuery(id+"F6.imprint","IMPRINT",EDGE,{"disambiguationData":[TD([[makeQuery(id+"F6.imprint","INTERSECT",VERTEX,{"disambiguationData":[OD(0.0)],"derivedFrom":[subQ0,sQuery(id+"F6.wireOp",EDGE,"E24.left")]}),1.0]])],"derivedFrom":subQ0})])],"isStart":true})});}
            var Q16;
            {var subQ0=sQuery(id+"F6.wireOp",EDGE,"E25.bottom");Q16=makeQuery(id+"F7.boolean.opBoolean","COPY",EDGE,{"derivedFrom":makeQuery(id+"F7.opExtrude","CAP_EDGE",EDGE,{"disambiguationData":[OSD([subQ0]),TDD([makeQuery(id+"F6.imprint","IMPRINT",EDGE,{"disambiguationData":[TD([[makeQuery(id+"F6.imprint","INTERSECT",VERTEX,{"disambiguationData":[OD(0.0)],"derivedFrom":[sQuery(id+"F6.wireOp",EDGE,"E20"),subQ0]}),-1.0]])],"derivedFrom":subQ0})])],"isStart":true})});}
            var Q17;
            {var subQ0=sQuery(id+"F6.wireOp",EDGE,"E20");Q17=makeQuery(id+"F7.boolean.opBoolean","COPY",EDGE,{"derivedFrom":makeQuery(id+"F7.opExtrude","CAP_EDGE",EDGE,{"disambiguationData":[OSD([subQ0]),TDD([makeQuery(id+"F6.imprint","IMPRINT",EDGE,{"disambiguationData":[TD([[makeQuery(id+"F6.imprint","INTERSECT",VERTEX,{"disambiguationData":[OD(0.0)],"derivedFrom":[subQ0,sQuery(id+"F6.wireOp",EDGE,"E25.bottom")]}),-1.0]])],"derivedFrom":subQ0})])],"isStart":true})});}
            var Q18;
            {var subQ0=sQuery(id+"F6.wireOp",EDGE,"E21");Q18=makeQuery(id+"F7.boolean.opBoolean","INTERSECT",EDGE,{"derivedFrom":[makeQuery(id+"F1.opRevolve","SWEPT_FACE",FACE,{"disambiguationData":[OSD([sQuery(id+"F0.wireOp",EDGE,"E0.bottom")])]}),makeQuery(id+"F7.opExtrude","SWEPT_FACE",FACE,{"disambiguationData":[OSD([subQ0]),TDD([makeQuery(id+"F6.imprint","IMPRINT",EDGE,{"disambiguationData":[TD([[makeQuery(id+"F6.imprint","INTERSECT",VERTEX,{"disambiguationData":[OD(0.0)],"derivedFrom":[subQ0,sQuery(id+"F6.wireOp",EDGE,"E24.right")]}),-1.0]])],"derivedFrom":subQ0})])]})]});}
            var Q19;
            {var subQ0=sQuery(id+"F6.wireOp",EDGE,"E25.bottom");Q19=makeQuery(id+"F7.boolean.opBoolean","INTERSECT",EDGE,{"derivedFrom":[makeQuery(id+"F1.opRevolve","SWEPT_FACE",FACE,{"disambiguationData":[OSD([sQuery(id+"F0.wireOp",EDGE,"E0.bottom")])]}),makeQuery(id+"F7.opExtrude","SWEPT_FACE",FACE,{"disambiguationData":[OSD([subQ0]),TDD([makeQuery(id+"F6.imprint","IMPRINT",EDGE,{"disambiguationData":[TD([[makeQuery(id+"F6.imprint","INTERSECT",VERTEX,{"disambiguationData":[OD(1.0)],"derivedFrom":[sQuery(id+"F6.wireOp",EDGE,"E20"),subQ0]}),1.0]])],"derivedFrom":subQ0})])]})]});}
            var Q20;
            {var subQ0=sQuery(id+"F6.wireOp",EDGE,"E20");Q20=makeQuery(id+"F7.boolean.opBoolean","INTERSECT",EDGE,{"derivedFrom":[makeQuery(id+"F1.opRevolve","SWEPT_FACE",FACE,{"disambiguationData":[OSD([sQuery(id+"F0.wireOp",EDGE,"E0.bottom")])]}),makeQuery(id+"F7.opExtrude","SWEPT_FACE",FACE,{"disambiguationData":[OSD([subQ0]),TDD([makeQuery(id+"F6.imprint","IMPRINT",EDGE,{"disambiguationData":[TD([[makeQuery(id+"F6.imprint","INTERSECT",VERTEX,{"disambiguationData":[OD(0.0)],"derivedFrom":[subQ0,sQuery(id+"F6.wireOp",EDGE,"E24.right")]}),-1.0]])],"derivedFrom":subQ0})])]})]});}
            var Q21;
            {var subQ0=sQuery(id+"F6.wireOp",EDGE,"E24.right");Q21=makeQuery(id+"F7.boolean.opBoolean","INTERSECT",EDGE,{"derivedFrom":[makeQuery(id+"F1.opRevolve","SWEPT_FACE",FACE,{"disambiguationData":[OSD([sQuery(id+"F0.wireOp",EDGE,"E0.bottom")])]}),makeQuery(id+"F7.opExtrude","SWEPT_FACE",FACE,{"disambiguationData":[OSD([subQ0]),TDD([makeQuery(id+"F6.imprint","IMPRINT",EDGE,{"disambiguationData":[TD([[makeQuery(id+"F6.imprint","INTERSECT",VERTEX,{"disambiguationData":[OD(0.0)],"derivedFrom":[sQuery(id+"F6.wireOp",EDGE,"E20"),subQ0]}),-1.0]])],"derivedFrom":subQ0})])]})]});}
            var Q22;
            {var subQ0=sQuery(id+"F6.wireOp",EDGE,"E24.left");Q22=makeQuery(id+"F7.boolean.opBoolean","INTERSECT",EDGE,{"derivedFrom":[makeQuery(id+"F1.opRevolve","SWEPT_FACE",FACE,{"disambiguationData":[OSD([sQuery(id+"F0.wireOp",EDGE,"E0.bottom")])]}),makeQuery(id+"F7.opExtrude","SWEPT_FACE",FACE,{"disambiguationData":[OSD([subQ0]),TDD([makeQuery(id+"F6.imprint","IMPRINT",EDGE,{"disambiguationData":[TD([[makeQuery(id+"F6.imprint","INTERSECT",VERTEX,{"disambiguationData":[OD(0.0)],"derivedFrom":[sQuery(id+"F6.wireOp",EDGE,"E20"),subQ0]}),-1.0]])],"derivedFrom":subQ0})])]})]});}
            var Q23;
            {var subQ0=sQuery(id+"F6.wireOp",EDGE,"E21");Q23=makeQuery(id+"F7.boolean.opBoolean","INTERSECT",EDGE,{"derivedFrom":[makeQuery(id+"F1.opRevolve","SWEPT_FACE",FACE,{"disambiguationData":[OSD([sQuery(id+"F0.wireOp",EDGE,"E0.bottom")])]}),makeQuery(id+"F7.opExtrude","SWEPT_FACE",FACE,{"disambiguationData":[OSD([subQ0]),TDD([makeQuery(id+"F6.imprint","IMPRINT",EDGE,{"disambiguationData":[TD([[makeQuery(id+"F6.imprint","INTERSECT",VERTEX,{"disambiguationData":[OD(0.0)],"derivedFrom":[subQ0,sQuery(id+"F6.wireOp",EDGE,"E24.left")]}),1.0]])],"derivedFrom":subQ0})])]})]});}
            var Q24;
            {var subQ0=sQuery(id+"F6.wireOp",EDGE,"E20");Q24=makeQuery(id+"F7.boolean.opBoolean","INTERSECT",EDGE,{"derivedFrom":[makeQuery(id+"F1.opRevolve","SWEPT_FACE",FACE,{"disambiguationData":[OSD([sQuery(id+"F0.wireOp",EDGE,"E0.bottom")])]}),makeQuery(id+"F7.opExtrude","SWEPT_FACE",FACE,{"disambiguationData":[OSD([subQ0]),TDD([makeQuery(id+"F6.imprint","IMPRINT",EDGE,{"disambiguationData":[TD([[makeQuery(id+"F6.imprint","INTERSECT",VERTEX,{"disambiguationData":[OD(0.0)],"derivedFrom":[subQ0,sQuery(id+"F6.wireOp",EDGE,"E25.bottom")]}),-1.0]])],"derivedFrom":subQ0})])]})]});}
            var Q25;
            {var subQ0=sQuery(id+"F6.wireOp",EDGE,"E25.bottom");Q25=makeQuery(id+"F7.boolean.opBoolean","INTERSECT",EDGE,{"derivedFrom":[makeQuery(id+"F1.opRevolve","SWEPT_FACE",FACE,{"disambiguationData":[OSD([sQuery(id+"F0.wireOp",EDGE,"E0.bottom")])]}),makeQuery(id+"F7.opExtrude","SWEPT_FACE",FACE,{"disambiguationData":[OSD([subQ0]),TDD([makeQuery(id+"F6.imprint","IMPRINT",EDGE,{"disambiguationData":[TD([[makeQuery(id+"F6.imprint","INTERSECT",VERTEX,{"disambiguationData":[OD(0.0)],"derivedFrom":[sQuery(id+"F6.wireOp",EDGE,"E20"),subQ0]}),-1.0]])],"derivedFrom":subQ0})])]})]});}
            var Q26;
            {var subQ0=sQuery(id+"F6.wireOp",EDGE,"E25.top");Q26=makeQuery(id+"F7.boolean.opBoolean","INTERSECT",EDGE,{"derivedFrom":[makeQuery(id+"F1.opRevolve","SWEPT_FACE",FACE,{"disambiguationData":[OSD([sQuery(id+"F0.wireOp",EDGE,"E0.bottom")])]}),makeQuery(id+"F7.opExtrude","SWEPT_FACE",FACE,{"disambiguationData":[OSD([subQ0]),TDD([makeQuery(id+"F6.imprint","IMPRINT",EDGE,{"disambiguationData":[TD([[makeQuery(id+"F6.imprint","INTERSECT",VERTEX,{"disambiguationData":[OD(1.0)],"derivedFrom":[sQuery(id+"F6.wireOp",EDGE,"E20"),subQ0]}),-1.0]])],"derivedFrom":subQ0})])]})]});}
            var Q27;
            {var subQ0=sQuery(id+"F6.wireOp",EDGE,"E20");Q27=makeQuery(id+"F7.boolean.opBoolean","INTERSECT",EDGE,{"derivedFrom":[makeQuery(id+"F1.opRevolve","SWEPT_FACE",FACE,{"disambiguationData":[OSD([sQuery(id+"F0.wireOp",EDGE,"E0.bottom")])]}),makeQuery(id+"F7.opExtrude","SWEPT_FACE",FACE,{"disambiguationData":[OSD([subQ0]),TDD([makeQuery(id+"F6.imprint","IMPRINT",EDGE,{"disambiguationData":[TD([[makeQuery(id+"F6.imprint","INTERSECT",VERTEX,{"disambiguationData":[OD(1.0)],"derivedFrom":[subQ0,sQuery(id+"F6.wireOp",EDGE,"E24.left")]}),-1.0]])],"derivedFrom":subQ0})])]})]});}
            var Q28;
            {var subQ0=sQuery(id+"F6.wireOp",EDGE,"E24.left");Q28=makeQuery(id+"F7.boolean.opBoolean","INTERSECT",EDGE,{"derivedFrom":[makeQuery(id+"F1.opRevolve","SWEPT_FACE",FACE,{"disambiguationData":[OSD([sQuery(id+"F0.wireOp",EDGE,"E0.bottom")])]}),makeQuery(id+"F7.opExtrude","SWEPT_FACE",FACE,{"disambiguationData":[OSD([subQ0]),TDD([makeQuery(id+"F6.imprint","IMPRINT",EDGE,{"disambiguationData":[TD([[makeQuery(id+"F6.imprint","INTERSECT",VERTEX,{"disambiguationData":[OD(1.0)],"derivedFrom":[sQuery(id+"F6.wireOp",EDGE,"E20"),subQ0]}),1.0]])],"derivedFrom":subQ0})])]})]});}
            var Q29;
            {var subQ0=sQuery(id+"F6.wireOp",EDGE,"E21");Q29=makeQuery(id+"F7.boolean.opBoolean","INTERSECT",EDGE,{"derivedFrom":[makeQuery(id+"F1.opRevolve","SWEPT_FACE",FACE,{"disambiguationData":[OSD([sQuery(id+"F0.wireOp",EDGE,"E0.bottom")])]}),makeQuery(id+"F7.opExtrude","SWEPT_FACE",FACE,{"disambiguationData":[OSD([subQ0]),TDD([makeQuery(id+"F6.imprint","IMPRINT",EDGE,{"disambiguationData":[TD([[makeQuery(id+"F6.imprint","INTERSECT",VERTEX,{"disambiguationData":[OD(1.0)],"derivedFrom":[subQ0,sQuery(id+"F6.wireOp",EDGE,"E24.left")]}),-1.0]])],"derivedFrom":subQ0})])]})]});}
            var Q30;
            {var subQ0=sQuery(id+"F6.wireOp",EDGE,"E21");Q30=makeQuery(id+"F7.boolean.opBoolean","INTERSECT",EDGE,{"derivedFrom":[makeQuery(id+"F1.opRevolve","SWEPT_FACE",FACE,{"disambiguationData":[OSD([sQuery(id+"F0.wireOp",EDGE,"E0.bottom")])]}),makeQuery(id+"F7.opExtrude","SWEPT_FACE",FACE,{"disambiguationData":[OSD([subQ0]),TDD([makeQuery(id+"F6.imprint","IMPRINT",EDGE,{"disambiguationData":[TD([[makeQuery(id+"F6.imprint","INTERSECT",VERTEX,{"disambiguationData":[OD(0.0)],"derivedFrom":[subQ0,sQuery(id+"F6.wireOp",EDGE,"E25.top")]}),-1.0]])],"derivedFrom":subQ0})])]})]});}
            var Q31;
            {var subQ0=sQuery(id+"F6.wireOp",EDGE,"E25.top");Q31=makeQuery(id+"F7.boolean.opBoolean","INTERSECT",EDGE,{"derivedFrom":[makeQuery(id+"F1.opRevolve","SWEPT_FACE",FACE,{"disambiguationData":[OSD([sQuery(id+"F0.wireOp",EDGE,"E0.bottom")])]}),makeQuery(id+"F7.opExtrude","SWEPT_FACE",FACE,{"disambiguationData":[OSD([subQ0]),TDD([makeQuery(id+"F6.imprint","IMPRINT",EDGE,{"disambiguationData":[TD([[makeQuery(id+"F6.imprint","INTERSECT",VERTEX,{"disambiguationData":[OD(0.0)],"derivedFrom":[sQuery(id+"F6.wireOp",EDGE,"E20"),subQ0]}),1.0]])],"derivedFrom":subQ0})])]})]});}
            var Q32;
            {var subQ0=sQuery(id+"F6.wireOp",EDGE,"E20");Q32=makeQuery(id+"F7.boolean.opBoolean","INTERSECT",EDGE,{"derivedFrom":[makeQuery(id+"F1.opRevolve","SWEPT_FACE",FACE,{"disambiguationData":[OSD([sQuery(id+"F0.wireOp",EDGE,"E0.bottom")])]}),makeQuery(id+"F7.opExtrude","SWEPT_FACE",FACE,{"disambiguationData":[OSD([subQ0]),TDD([makeQuery(id+"F6.imprint","IMPRINT",EDGE,{"disambiguationData":[TD([[makeQuery(id+"F6.imprint","INTERSECT",VERTEX,{"disambiguationData":[OD(0.0)],"derivedFrom":[subQ0,sQuery(id+"F6.wireOp",EDGE,"E25.top")]}),-1.0]])],"derivedFrom":subQ0})])]})]});}
            var Q33;
            {var subQ0=sQuery(id+"F6.wireOp",EDGE,"E24.right");Q33=makeQuery(id+"F7.boolean.opBoolean","INTERSECT",EDGE,{"derivedFrom":[makeQuery(id+"F1.opRevolve","SWEPT_FACE",FACE,{"disambiguationData":[OSD([sQuery(id+"F0.wireOp",EDGE,"E0.bottom")])]}),makeQuery(id+"F7.opExtrude","SWEPT_FACE",FACE,{"disambiguationData":[OSD([subQ0]),TDD([makeQuery(id+"F6.imprint","IMPRINT",EDGE,{"disambiguationData":[TD([[makeQuery(id+"F6.imprint","INTERSECT",VERTEX,{"disambiguationData":[OD(1.0)],"derivedFrom":[sQuery(id+"F6.wireOp",EDGE,"E20"),subQ0]}),1.0]])],"derivedFrom":subQ0})])]})]});}
            fillet(context, id + "F8", {"entities" : qUnion([Q0, Q1, Q2, Q3, Q4, Q5, Q6, Q7, Q8, Q9, Q10, Q11, Q12, Q13, Q14, Q15, Q16, Q17, Q18, Q19, Q20, Q21, Q22, Q23, Q24, Q25, Q26, Q27, Q28, Q29, Q30, Q31, Q32, Q33]), "radius" : 1 * mm, "tangentPropagation" : true, "allowEdgeOverflow" : false});
        }
    });
